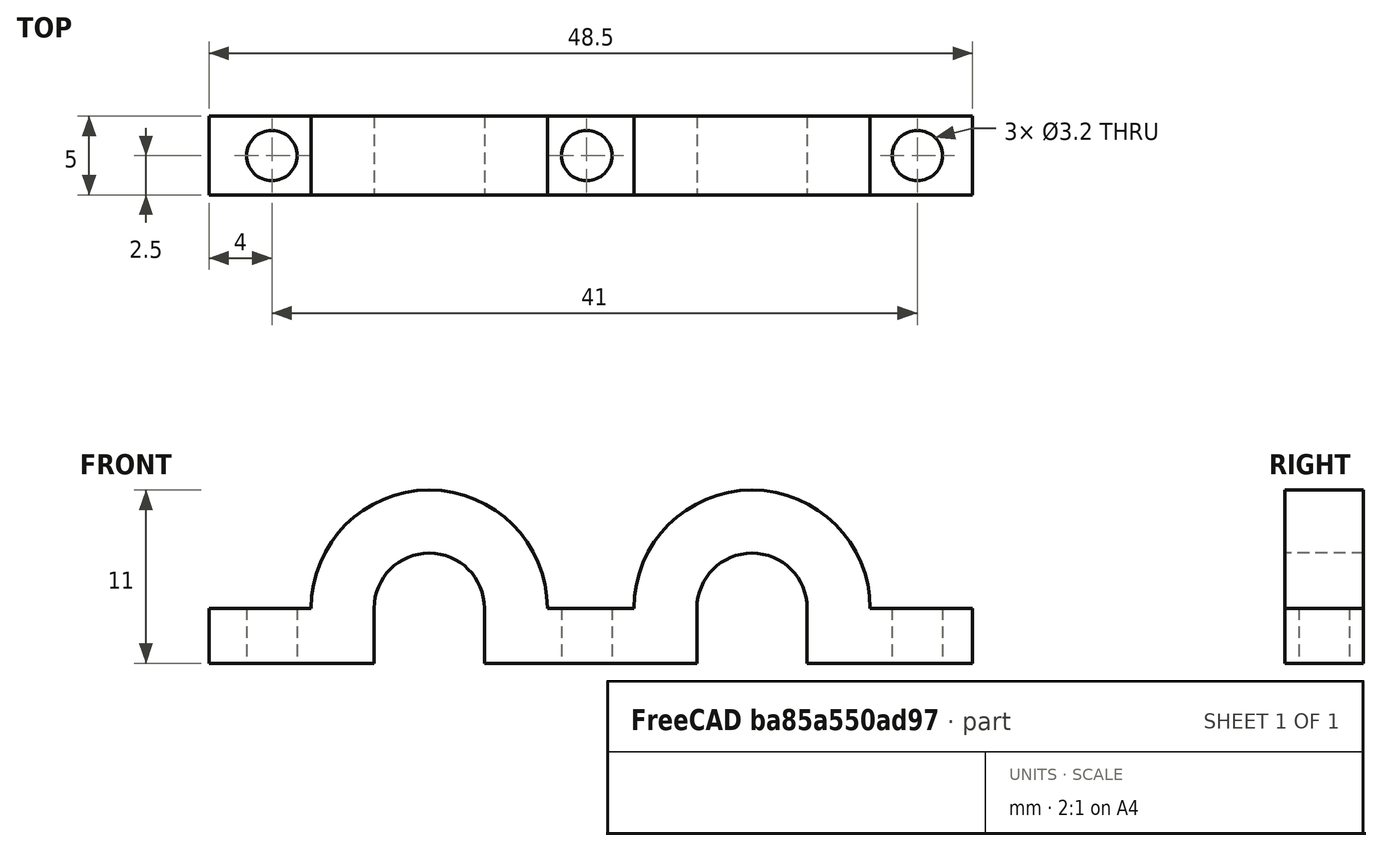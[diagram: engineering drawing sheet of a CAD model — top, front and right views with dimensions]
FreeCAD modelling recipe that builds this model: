
FCSTD DOCUMENT  (FreeCAD 0.18R16110 (Git))
Label: tube-mount-6mm
License: All rights reserved
LicenseURL: http://en.wikipedia.org/wiki/All_rights_reserved
objects: Part::Cylinder×5, Part::Cut×5, Part::Box×3, Part::MultiFuse×1, Mesh::Feature×1
note: 14 computed .brp shape members not serialized (recipe doc carries the construction recipe); baked Part::Feature solids carry a one-line shape summary decoded from their .brp

FEATURE [Part::Box] Box043  label="Quader037"
  AttacherType = Attacher::AttachEngine3D
  Height = 5
  Length = 10.5
  Placement = pos=(24,-3.5,0) rot=(0,0,1;0rad)
  Width = 3.5
FEATURE [Part::Box] Box042  label="Quader036"
  AttacherType = Attacher::AttachEngine3D
  Height = 5
  Length = 13.5
  Placement = pos=(3.5,-3.5,0) rot=(0,0,1;0rad)
  Width = 3.5
FEATURE [Part::Cylinder] Cylinder117  label="Zylinder090"
  Angle = 360
  AttacherType = Attacher::AttachEngine3D
  Height = 10
  Radius = 3.5
FEATURE [Part::Cylinder] Cylinder126  label="Zylinder099"
  Angle = 360
  AttacherType = Attacher::AttachEngine3D
  Height = 10
  Placement = pos=(10,2,2.5) rot=(1,0,0;1.5708rad)
  Radius = 1.6
FEATURE [Part::Cylinder] Cylinder125  label="Zylinder098"
  Angle = 360
  AttacherType = Attacher::AttachEngine3D
  Height = 10
  Placement = pos=(31,2,2.5) rot=(1,0,0;1.5708rad)
  Radius = 1.6
FEATURE [Part::Box] Box041  label="Quader035"
  AttacherType = Attacher::AttachEngine3D
  Height = 5
  Length = 10.5
  Placement = pos=(-14,-3.5,0) rot=(0,0,1;0rad)
  Width = 3.5
FEATURE [Part::Cylinder] Cylinder118  label="Zylinder091"
  Angle = 180
  AttacherType = Attacher::AttachEngine3D
  Height = 5
  Radius = 7.5
FEATURE [Part::Cut] Cut150
  Base = -> Cylinder118
  Placement = pos=(20.5,0,0) rot=(0,0,1;0rad)
  Tool = -> Cylinder117
FEATURE [Part::Cut] Cut149
  Base = -> Cylinder118
  Tool = -> Cylinder117
FEATURE [Part::MultiFuse] Fusion017  label="Schlauchhalterung"
  Shapes = -> [Box041,Box043,Box042,Cut150,Cut149]
FEATURE [Part::Cylinder] Cylinder123  label="Zylinder096"
  Angle = 360
  AttacherType = Attacher::AttachEngine3D
  Height = 10
  Placement = pos=(-10,2,2.5) rot=(1,0,0;1.5708rad)
  Radius = 1.6
FEATURE [Part::Cut] Cut153
  Base = -> Fusion017
  Tool = -> Cylinder123
FEATURE [Part::Cut] Cut154
  Base = -> Cut153
  Tool = -> Cylinder126
FEATURE [Part::Cut] Cut155  label="tube-mount-6mm"
  Base = -> Cut154
  Placement = pos=(-145,25,-36) rot=(1,0,0;1.5708rad)
  Tool = -> Cylinder125
FEATURE [Mesh::Feature] Mesh  label="tube-mount-6mm (Meshed)"
